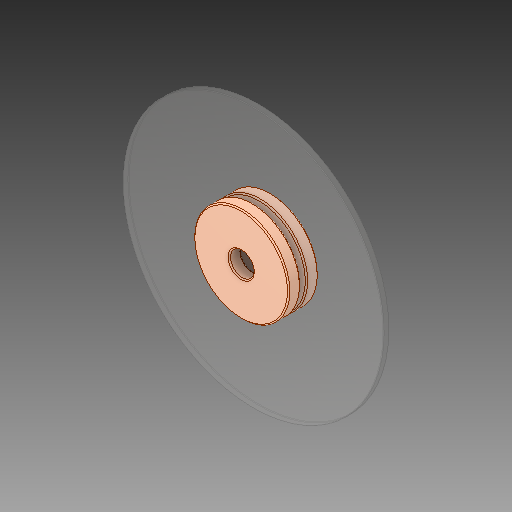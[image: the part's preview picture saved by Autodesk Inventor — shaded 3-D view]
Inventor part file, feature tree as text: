
AUTODESK INVENTOR PART (.ipt)
format: ipt  version: 2019 (Build 230136000, 136)  size: 179,200 bytes
history: mixed  units: mm
features: other x3, fillet x3, imported_body x1
ambient origin geometry x8: Origin, YZ Plane, XZ Plane, XY Plane, X Axis, Y Axis, Z Axis, Center Point
bodies: Body1 (imported_parasolid), Body2 (imported_parasolid), Body3 (imported_parasolid)
feature tree (7):
  other  "Твердое тело1"
  other  "Твердое тело2"
  other  "Твердое тело3"
  fillet  "Fillet1"  [1 undecoded]
  fillet  "Fillet2"  [1 undecoded]
  fillet  "Fillet3"  [1 undecoded]
  imported_body  NMx_Import_Brep_tag  [imported B-rep: ~21 faces, bbox_mm=[15.0, 0.0, 2.5]]
note: 3 required parameter values undecoded (feature->parameter linkage not recoverable at this tier; creation-order binding heuristic only, values carry confidence <= 0.55)
